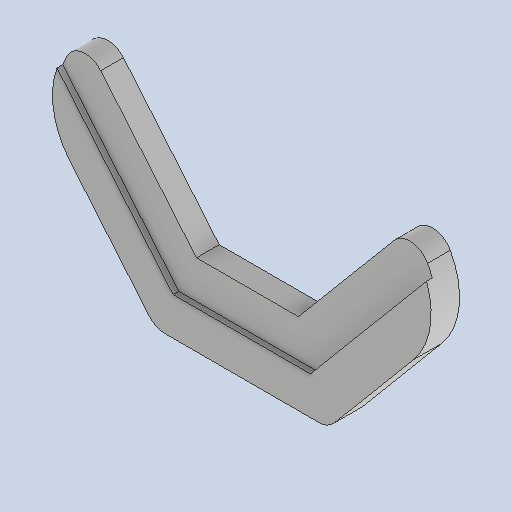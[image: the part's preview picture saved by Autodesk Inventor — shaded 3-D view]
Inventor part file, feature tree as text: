
AUTODESK INVENTOR PART (.ipt)
format: ipt  version: 2025 (Build 290162010, 162A)  size: 315,904 bytes
history: native  units: mm
features: extrude x2, other x2, sketch x2, fillet x1, projected_geometry x1
ambient origin geometry x8: Origin, YZ Plane, XZ Plane, XY Plane, X Axis, Y Axis, Z Axis, Center Point
bodies: Solid1 (feature_tree)
feature tree (8):
  extrude  "Extrusion1"  Depth=40.0mm
  extrude  "Extrusion2"  Depth=15.0mm TaperAngle=0.0deg
  fillet  "Fillet1"  Radius=20.0mm
  other  "A-Side Definition"
  sketch  "Sketch1"  dims[d1=53.9mm d3=40.0mm]
  sketch  "Sketch2"  dims[d5=40.0mm d6=15.0mm d7=0.0mm d8=20.0mm d9=20.0mm d10=20.0mm d11=3.0mm d12=0.0mm d16=22.68928mm d17=70.0mm d18=10.7mm]
  projected_geometry  "Projected Loop1"
  other  "Definition1"
